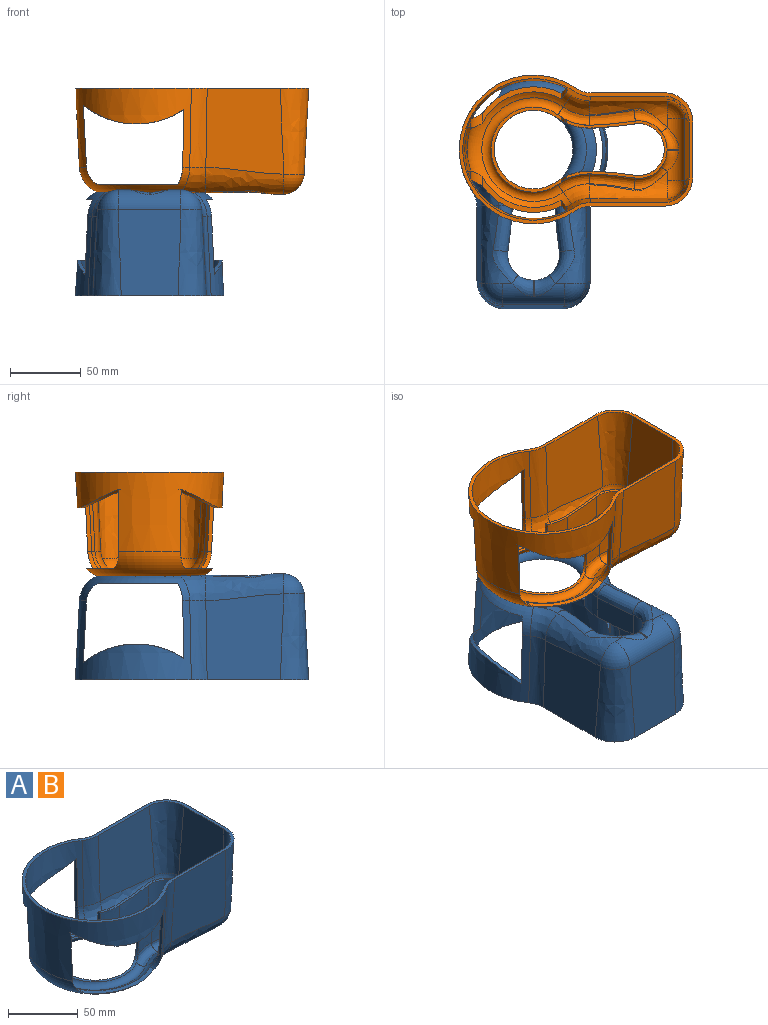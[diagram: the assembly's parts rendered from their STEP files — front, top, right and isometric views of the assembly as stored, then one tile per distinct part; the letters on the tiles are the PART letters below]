
ASSEMBLY  parts=2 mates=1
PART A: 85 faces, bbox 171.8x112.6x183.9 mm
  f0: torus R=34.71mm, axis (0,0,-1), area 1131.2mm2, adj f1,f2,f30,f69
  f1: bspline ~23.53x13.12mm, area 217.3mm2, adj f0,f28,f37,f52,f69,f70
  f2: bspline ~23.61x13.12mm, area 217.3mm2, adj f0,f33,f40,f53,f68,f69
  f3: bspline ~25.23x15.77mm, area 312.9mm2, adj f4,f12,f43,f63,f69,f70
  f4: torus R=34.71mm, axis (0,0,1), area 1706.2mm2, adj f3,f5,f15,f69
  f5: bspline ~26.78x15.89mm, area 313mm2, adj f4,f18,f48,f67,f68,f69
  f6: plane 166.19x106.19mm, normal (0,0,1), area 1128.8mm2, adj f7,f8,f9,f10,f11,f13,f16,f22
  f7: plane 61.19x55.22mm, normal (0,-1,-0.05), area 3118.2mm2, adj f6,f16,f20,f22
  f8: cone r=50mm half-angle=3deg, axis (0,0,1), area 6740.4mm2, adj f6,f11,f15,f16,f73,f74,f75,f77
  f9: plane 61.19x55.22mm, normal (0,1,-0.05), area 3118.2mm2, adj f6,f11,f13,f14
  f10: plane 61.19x45.06mm, normal (1,0,-0.05), area 2568mm2, adj f6,f13,f19,f22
  f11: bspline ~178.78x14.62mm, area 674.8mm2, adj f6,f8,f9,f12
  f12: bspline ~29.47x24.95mm, area 334mm2, adj f3,f11,f14,f15
  f13: bspline ~62.61x21.05mm, area 1661.9mm2, adj f6,f9,f10,f17
  f14: bspline ~54.64x49.1mm, area 1134.4mm2, adj f9,f12,f17,f19,f61,f63
  f15: torus R=29.71mm, axis (0,0,1), area 2447.5mm2, adj f4,f8,f12,f18,f74,f75,f76,f81
  f16: bspline ~178.78x14.62mm, area 674.8mm2, adj f6,f7,f8,f18
  f17: sphere r=15mm, area 213.9mm2, adj f13,f14,f19
  f18: bspline ~29.49x24.28mm, area 334mm2, adj f5,f15,f16,f20
  f19: cylinder r=15mm len=43.91mm, axis (0,1,0), area 791mm2, adj f10,f14,f17,f20,f21,f62,f64,f65
  f20: bspline ~55.19x49.1mm, area 1134.1mm2, adj f7,f18,f19,f21,f66,f67
  f21: sphere r=15mm, area 329.9mm2, adj f19,f20,f22
  f22: bspline ~62.61x21.05mm, area 1661.9mm2, adj f6,f7,f10,f21
  f23: plane 60.68x54.86mm, normal (0,1,0.05), area 3111.4mm2, adj f6,f31,f36
  f24: cone r=47.5mm half-angle=3deg, axis (0,0,1), area 5858.1mm2, adj f6,f27,f30,f31,f73,f75,f77,f78
  f25: plane 60.68x54.86mm, normal (0,-1,0.05), area 3111.4mm2, adj f6,f27,f29
  f26: plane 60.68x44.34mm, normal (-1,0,0.05), area 2562.7mm2, adj f6,f29,f34,f36
  f27: bspline ~178.79x16.08mm, area 757.4mm2, adj f6,f24,f25,f28
  f28: bspline ~29.47x23.07mm, area 309.5mm2, adj f1,f27,f30
  f29: offset ~70.11x26.18mm, area 1420.1mm2, adj f6,f25,f26,f32
  f30: torus R=29.71mm, axis (0,0,1), area 1437.7mm2, adj f0,f24,f28,f33,f73,f74,f75,f76
  f31: bspline ~178.79x16.08mm, area 757.4mm2, adj f6,f23,f24,f33
  f32: sphere r=12.5mm, area 232.6mm2, adj f29,f34
  f33: bspline ~29.49x22.33mm, area 309.5mm2, adj f2,f30,f31
  f34: cylinder r=12.5mm len=43.91mm, axis (0,1,0), area 645.9mm2, adj f26,f32,f35,f56,f57,f58,f59,f60
  f35: sphere r=12.5mm, area 232.6mm2, adj f34,f36
  f36: offset ~65.96x25.1mm, area 1420.1mm2, adj f6,f23,f26,f35
  f37: extruded ~18.98x16.46mm, area 293mm2, adj f1,f38,f42,f70,f72
  f38: extruded ~32.14x16.46mm, area 524.7mm2, adj f37,f39,f42,f52
  f39: cylinder r=20mm len=22.5mm, axis (0,0,1), area 565.9mm2, adj f38,f42,f50,f54,f56
  f40: extruded ~18.98x16.46mm, area 293mm2, adj f2,f41,f42,f68,f71
  f41: extruded ~32.14x16.46mm, area 524.7mm2, adj f40,f42,f51,f53
  f42: plane 70.94x41.38mm, normal (0,0,1), area 327.1mm2, adj f37,f38,f39,f40,f41,f43,f44,f45
  f43: extruded ~19.29x17mm, area 303.9mm2, adj f3,f42,f44,f70,f72
  f44: extruded ~32.39x17mm, area 547.2mm2, adj f42,f43,f45,f63
  f45: cylinder r=18mm len=20.25mm, axis (0,0,1), area 526.3mm2, adj f42,f44,f46,f61,f62
  f46: plane 16.25x0.73mm, normal (-1,0,0), area 11.8mm2, adj f42,f45,f47,f64
  f47: cylinder r=18mm len=20.25mm, axis (0,0,1), area 526.3mm2, adj f42,f46,f49,f65,f66
  f48: extruded ~19.29x17mm, area 303.9mm2, adj f5,f42,f49,f68,f71
  f49: extruded ~32.39x17mm, area 547.2mm2, adj f42,f47,f48,f67
  f50: plane 15.59x0.73mm, normal (1,0,0), area 11.3mm2, adj f39,f42,f51,f58,f59,f60
  f51: cylinder r=20mm len=22.5mm, axis (0,0,1), area 565.9mm2, adj f41,f42,f50,f55,f57
  f52: bspline ~38.62x11.5mm, area 326.4mm2, adj f1,f38,f54
  f53: bspline ~38.62x11.5mm, area 326.4mm2, adj f2,f41,f55
  f54: bspline ~27.29x17.39mm, area 213mm2, adj f39,f52,f56
  f55: bspline ~25.43x17.39mm, area 213mm2, adj f51,f53,f57
  f56: bspline ~18.19x13.17mm, area 147.7mm2, adj f34,f39,f54,f58
  f57: bspline ~18.19x13.17mm, area 147.7mm2, adj f34,f51,f55,f59
  f58: cylinder r=5mm len=8.33mm, axis (0,1,0), area 0mm2, adj f34,f50,f56,f60
  f59: cylinder r=5mm len=8.33mm, axis (0,1,0), area 0mm2, adj f34,f50,f57,f60
  f60: cylinder r=5mm len=8.33mm, axis (0,1,0), area 8.3mm2, adj f34,f50,f58,f59
  f61: bspline ~26.91x18.74mm, area 280.4mm2, adj f14,f45,f62,f63
  f62: bspline ~17.65x15.24mm, area 193.9mm2, adj f19,f45,f61,f64
  f63: bspline ~52.16x14.06mm, area 454.1mm2, adj f3,f14,f44,f61
  f64: cylinder r=7mm len=11.38mm, axis (0,1,0), area 11.4mm2, adj f19,f46,f62,f65
  f65: bspline ~18.35x15.87mm, area 193.9mm2, adj f19,f47,f64,f66
  f66: bspline ~25.98x18.44mm, area 280.4mm2, adj f20,f47,f65,f67
  f67: bspline ~37.72x14.33mm, area 454.1mm2, adj f5,f20,f49,f66
  f68: extruded ~12.54x4.72mm, area 29.9mm2, adj f2,f5,f40,f48,f69,f71
  f69: plane 60.29x49.62mm, normal (0,0,1), area 301.8mm2, adj f0,f1,f2,f3,f4,f5,f68,f70
  f70: extruded ~12.54x4.72mm, area 29.9mm2, adj f1,f3,f37,f43,f69,f72
  f71: extruded ~5.92x2.23mm, area 12.9mm2, adj f40,f42,f48,f68
  f72: extruded ~5.92x2.23mm, area 12.9mm2, adj f37,f42,f43,f70
  f73: extruded ~40.92x4.85mm, area 116.9mm2, adj f8,f24,f30,f74,f78
  f74: extruded ~12.54x7.87mm, area 43.1mm2, adj f8,f15,f30,f73,f76
  f75: cylinder r=15mm len=12.68mm, axis (0,-1,0), area 107.3mm2, adj f8,f15,f24,f30,f76,f77
  f76: plane 55.79x25.73mm, normal (0,0,1), area 230mm2, adj f15,f30,f74,f75
  f77: plane 43.79x7.1mm, normal (1,0,0.05), area 291.4mm2, adj f8,f24,f75,f78
  f78: cylinder r=60mm len=71.21mm, axis (0,-1,0), area 233mm2, adj f8,f24,f73,f77
  f79: cylinder r=60mm len=71.21mm, axis (0,-1,0), area 233mm2, adj f8,f24,f80,f82
  f80: plane 43.79x7.1mm, normal (1,0,0.05), area 291.4mm2, adj f8,f24,f79,f81
  f81: cylinder r=15mm len=12.68mm, axis (0,-1,0), area 107.3mm2, adj f8,f15,f24,f30,f80,f83
  f82: extruded ~40.92x4.85mm, area 116.9mm2, adj f8,f24,f30,f79,f84
  f83: plane 55.79x25.73mm, normal (0,0,1), area 230mm2, adj f15,f30,f81,f84
  f84: extruded ~12.54x7.87mm, area 43.1mm2, adj f8,f15,f30,f82,f83
PART B: same geometry as A
PLACE A rot(axis=(0.71,-0.71,0),180deg) t=(-30.69,0.19,-60.25)mm
PLACE B t=(-30.69,0.19,-13.33)mm
MATE parallel A.f0 <-> B.f0  axis (0,0,-1) through (-30.69,0.19,-36.79)mm
